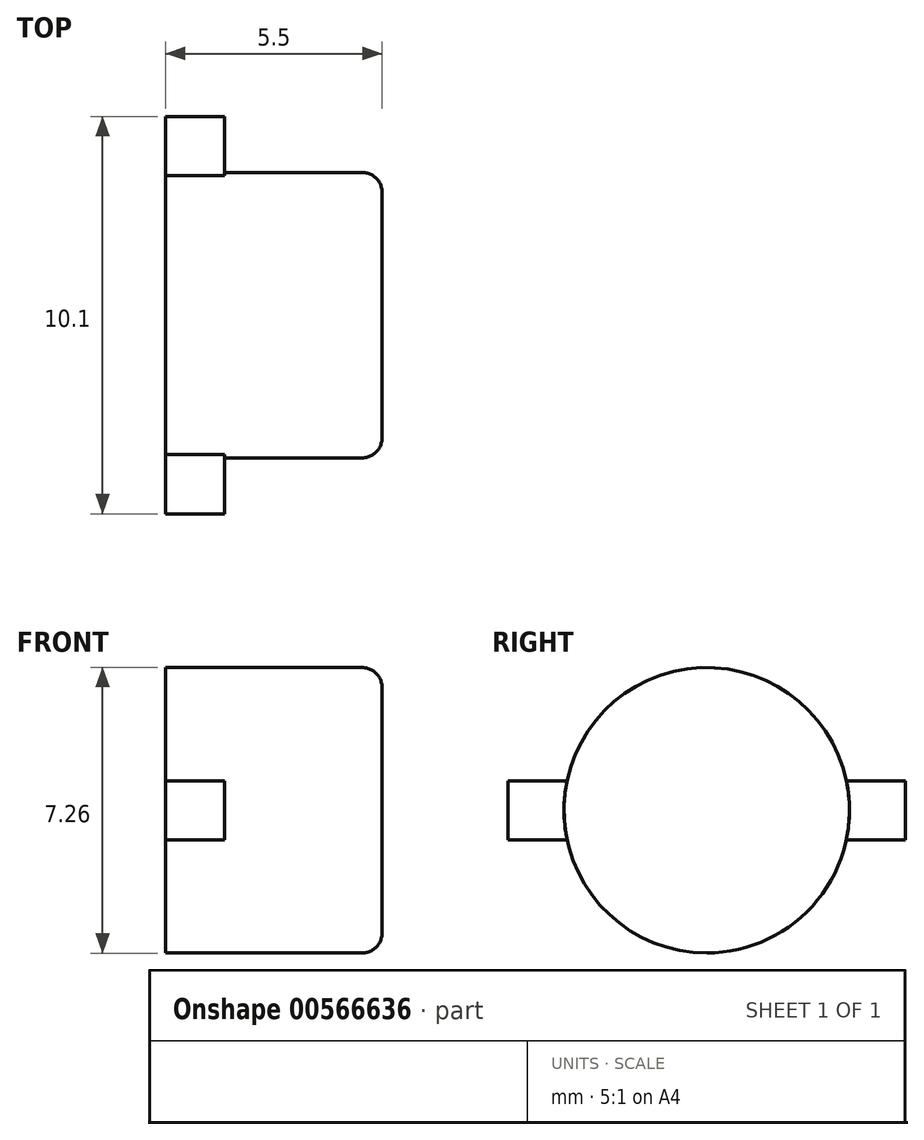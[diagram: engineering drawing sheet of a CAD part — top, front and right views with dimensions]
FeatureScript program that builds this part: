
annotation { "Feature Type Name" : "Feature", "Feature Type Description" : "" }
export const myFeature = defineFeature(function(context is Context, id is Id, definition is map)
    precondition{}
    {
        {
            var Q0;
            Q0=qCreatedBy(makeId("Right.planeOp"),FACE);
            var sketch = newSketch(context, id + "F0", { "sketchPlane" : qUnion([Q0])});
            skCircle(sketch, "E0", {"center": v(0, 0) * mm, "radius": 3.62 * mm});
            skSolve(sketch);
        }
        {
            var Q0;
            Q0=makeQuery(id+"F0.imprint","IMPRINT",FACE,{"disambiguationData":[TD([[makeQuery(id+"F0.imprint","IMPRINT",EDGE,{"derivedFrom":sQuery(id+"F0.wireOp",EDGE,"E0")}),1.0]])]});
            extrude(context, id + "F1", {"entities" : qUnion([Q0]), "endBound" : BoundingType.SYMMETRIC, "depth" : 5.5 * mm, "offsetDistance" : 25 * mm});
        }
        {
            var Q0;
            Q0=makeQuery(id+"F1.opExtrude","CAP_FACE",FACE,{"disambiguationData":[OSD([sQuery(id+"F0.wireOp",EDGE,"E0")])],"isStart":false});
            fillet(context, id + "F2", {"entities" : qUnion([Q0]), "radius" : 0.5 * mm, "tangentPropagation" : true, "allowEdgeOverflow" : false});
        }
        {
            var Q0;
            Q0=makeQuery(id+"F1.opExtrude","CAP_FACE",FACE,{"disambiguationData":[OSD([sQuery(id+"F0.wireOp",EDGE,"E0")])],"isStart":true});
            var sketch = newSketch(context, id + "F3", { "sketchPlane" : qUnion([Q0])});
            skLineSegment(sketch, "E1.left", {"start": v(5.05, -0.75) * mm, "end": v(5.05, 0.75) * mm});
            skLineSegment(sketch, "E2.left", {"start": v(-5.05, 0.75) * mm, "end": v(-5.05, -0.75) * mm});
            skLineSegment(sketch, "E3", {"start": v(5.05, 0.75) * mm, "end": v(3.55, 0.75) * mm});
            skLineSegment(sketch, "E4", {"start": v(5.05, -0.75) * mm, "end": v(3.55, -0.75) * mm});
            skArc(sketch, "E5", {"start": v(-3.55, 0.75) * mm, "mid": v(-3.63, 0) * mm, "end": v(-3.55, -0.75) * mm});
            skLineSegment(sketch, "E6", {"start": v(-5.05, 0.75) * mm, "end": v(-3.55, 0.75) * mm});
            skLineSegment(sketch, "E7", {"start": v(-5.05, -0.75) * mm, "end": v(-3.55, -0.75) * mm});
            skArc(sketch, "E8.trimOffspring", {"start": v(3.55, -0.75) * mm, "mid": v(3.63, 0) * mm, "end": v(3.55, 0.75) * mm});
            skPoint(sketch, "E9", {"position": v(5.05, 0) * mm});
            skPoint(sketch, "E10", {"position": v(-5.05, 0) * mm});
            skSolve(sketch);
        }
        {
            var Q0;
            Q0=qSketchRegion(id+"F3",true);
            extrude(context, id + "F4", {"entities" : qUnion([Q0]), "operationType" : NewBodyOperationType.ADD, "oppositeDirection" : true, "depth" : 1.5 * mm, "offsetDistance" : 25 * mm});
        }
    });
